FCSTD DOCUMENT  (FreeCAD 0.19R)
Label: CNC_v3
License: All rights reserved
LicenseURL: http://en.wikipedia.org/wiki/All_rights_reserved
objects: Sketcher::SketchObject×1, PartDesign::Body×1
note: 2 computed .brp shape members not serialized (recipe doc carries the construction recipe); baked Part::Feature solids carry a one-line shape summary decoded from their .brp

FEATURE [Sketcher::SketchObject] Sketch
  FullyConstrained = false
  MapMode = 5
  Support = -> [XY_Plane]
  sketch-geometry (24):
    g0: LineSegment StartX=-478.539 StartY=238.533 StartZ=0 EndX=331.461 EndY=238.533 EndZ=0
    g1: LineSegment StartX=331.461 StartY=238.533 StartZ=0 EndX=331.461 EndY=-261.467 EndZ=0
    g2: LineSegment StartX=331.461 StartY=-261.467 StartZ=0 EndX=-478.539 EndY=-261.467 EndZ=0
    g3: LineSegment StartX=-478.539 StartY=-261.467 StartZ=0 EndX=-478.539 EndY=238.533 EndZ=0
    g4: Circle CenterX=-442.539 CenterY=-225.467 CenterZ=0 NormalX=0 NormalY=0 NormalZ=1 AngleXU=0 Radius=3
    g5: Circle CenterX=-442.539 CenterY=-197.467 CenterZ=0 NormalX=0 NormalY=0 NormalZ=1 AngleXU=0 Radius=3
    g6: Circle CenterX=-414.539 CenterY=-225.467 CenterZ=0 NormalX=0 NormalY=0 NormalZ=1 AngleXU=0 Radius=3
    g7: Circle CenterX=-414.539 CenterY=-197.467 CenterZ=0 NormalX=0 NormalY=0 NormalZ=1 AngleXU=0 Radius=3
    g8: Circle CenterX=-386.539 CenterY=-225.467 CenterZ=0 NormalX=0 NormalY=0 NormalZ=1 AngleXU=0 Radius=3
    g9: Circle CenterX=-386.539 CenterY=-197.467 CenterZ=0 NormalX=0 NormalY=0 NormalZ=1 AngleXU=0 Radius=3
    g10: Circle CenterX=89.4612 CenterY=-225.467 CenterZ=0 NormalX=0 NormalY=0 NormalZ=1 AngleXU=0 Radius=3
    g11: Circle CenterX=89.4612 CenterY=-197.467 CenterZ=0 NormalX=0 NormalY=0 NormalZ=1 AngleXU=0 Radius=3
    g12: Circle CenterX=117.461 CenterY=-225.467 CenterZ=0 NormalX=0 NormalY=0 NormalZ=1 AngleXU=0 Radius=3
    g13: Circle CenterX=117.461 CenterY=-197.467 CenterZ=0 NormalX=0 NormalY=0 NormalZ=1 AngleXU=0 Radius=3
    g14: Circle CenterX=-442.539 CenterY=72.8313 CenterZ=0 NormalX=0 NormalY=0 NormalZ=1 AngleXU=0 Radius=3
    g15: Circle CenterX=-442.539 CenterY=100.831 CenterZ=0 NormalX=0 NormalY=0 NormalZ=1 AngleXU=0 Radius=3
    g16: Circle CenterX=-414.539 CenterY=72.8313 CenterZ=0 NormalX=0 NormalY=0 NormalZ=1 AngleXU=0 Radius=3
    g17: Circle CenterX=-414.539 CenterY=100.831 CenterZ=0 NormalX=0 NormalY=0 NormalZ=1 AngleXU=0 Radius=3
    g18: Circle CenterX=-386.539 CenterY=72.8313 CenterZ=0 NormalX=0 NormalY=0 NormalZ=1 AngleXU=0 Radius=3
    g19: Circle CenterX=-386.539 CenterY=100.831 CenterZ=0 NormalX=0 NormalY=0 NormalZ=1 AngleXU=0 Radius=3
    g20: Circle CenterX=89.4612 CenterY=75.2161 CenterZ=0 NormalX=0 NormalY=0 NormalZ=1 AngleXU=0 Radius=3
    g21: Circle CenterX=89.4612 CenterY=103.216 CenterZ=0 NormalX=0 NormalY=0 NormalZ=1 AngleXU=0 Radius=3
    g22: Circle CenterX=117.461 CenterY=74.9988 CenterZ=0 NormalX=0 NormalY=0 NormalZ=1 AngleXU=0 Radius=3
    g23: Circle CenterX=117.461 CenterY=102.999 CenterZ=0 NormalX=0 NormalY=0 NormalZ=1 AngleXU=0 Radius=3
  constraints (59):
    c: Coincident(g0,g1)
    c: Coincident(g1,g2)
    c: Coincident(g2,g3)
    c: Coincident(g3,g0)
    c: Horizontal(g0)
    c: Horizontal(g2)
    c: Vertical(g1)
    c: Vertical(g3)
    c: DistanceX(g2,g2) = 810
    c: DistanceY(g1,g1) = 500
    c: Radius(g4) = 3
    c: Equal(g4,g5) = 3
    c: Equal(g4,g6) = 3
    c: Equal(g6,g7) = 3
    c: Equal(g8,g9) = 3
    c: Equal(g10,g11) = 3
    c: Equal(g12,g13) = 3
    c: Distance(g4,g2) = 36
    c: Distance(g4,g3) = 36
    c: DistanceY(g4,g5) = 28
    c: DistanceX(g5,g7) = 28
    c: DistanceX(g7,g9) = 28
    c: DistanceY(g12,g13) = 28
    c: DistanceX(g11,g13) = 28
    c: DistanceX(g10,g12) = 28
    c: Equal(g4,g14) = 3
    c: Equal(g14,g15) = 3
    c: Equal(g14,g16) = 3
    c: Equal(g16,g17) = 3
    c: Equal(g18,g19) = 3
    c: Equal(g20,g21) = 3
    c: Equal(g22,g23) = 3
    c: DistanceY(g14,g15) = 28
    c: DistanceX(g15,g17) = 28
    c: DistanceX(g17,g19) = 28
    c: DistanceY(g22,g23) = 28
    c: DistanceX(g21,g23) = 28
    c: DistanceX(g20,g22) = 28
    c: Distance(g15,g3) = 36
    c: Distance(g14,g3) = 36
    c: DistanceX(g14,g16) = 28
    c: DistanceX(g16,g18) = 28
    c: DistanceY(g16,g17) = 28
    c: DistanceY(g18,g19) = 28
    c: DistanceY(g20,g21) = 28
    c: DistanceX(g4,g6) = 28
    c: DistanceX(g6,g8) = 28
    c: DistanceY(g6,g7) = 28
    c: DistanceY(g8,g9) = 28
    c: DistanceY(g10,g11) = 28
    c: Distance(g10,g2) = 36
    c: Distance(g12,g2) = 36
    c: Distance(g6,g2) = 36
    c: Distance(g8,g2) = 36
    c: DistanceX(g7,g13) = 532
    c: DistanceX(g6,g12) = 532
    c: Distance(g5,g3) = 36
    c: DistanceX(g17,g23) = 532
    c: DistanceX(g16,g22) = 532
FEATURE [PartDesign::Body] Body
  Group = -> [Sketch]
  Origin = -> Origin
